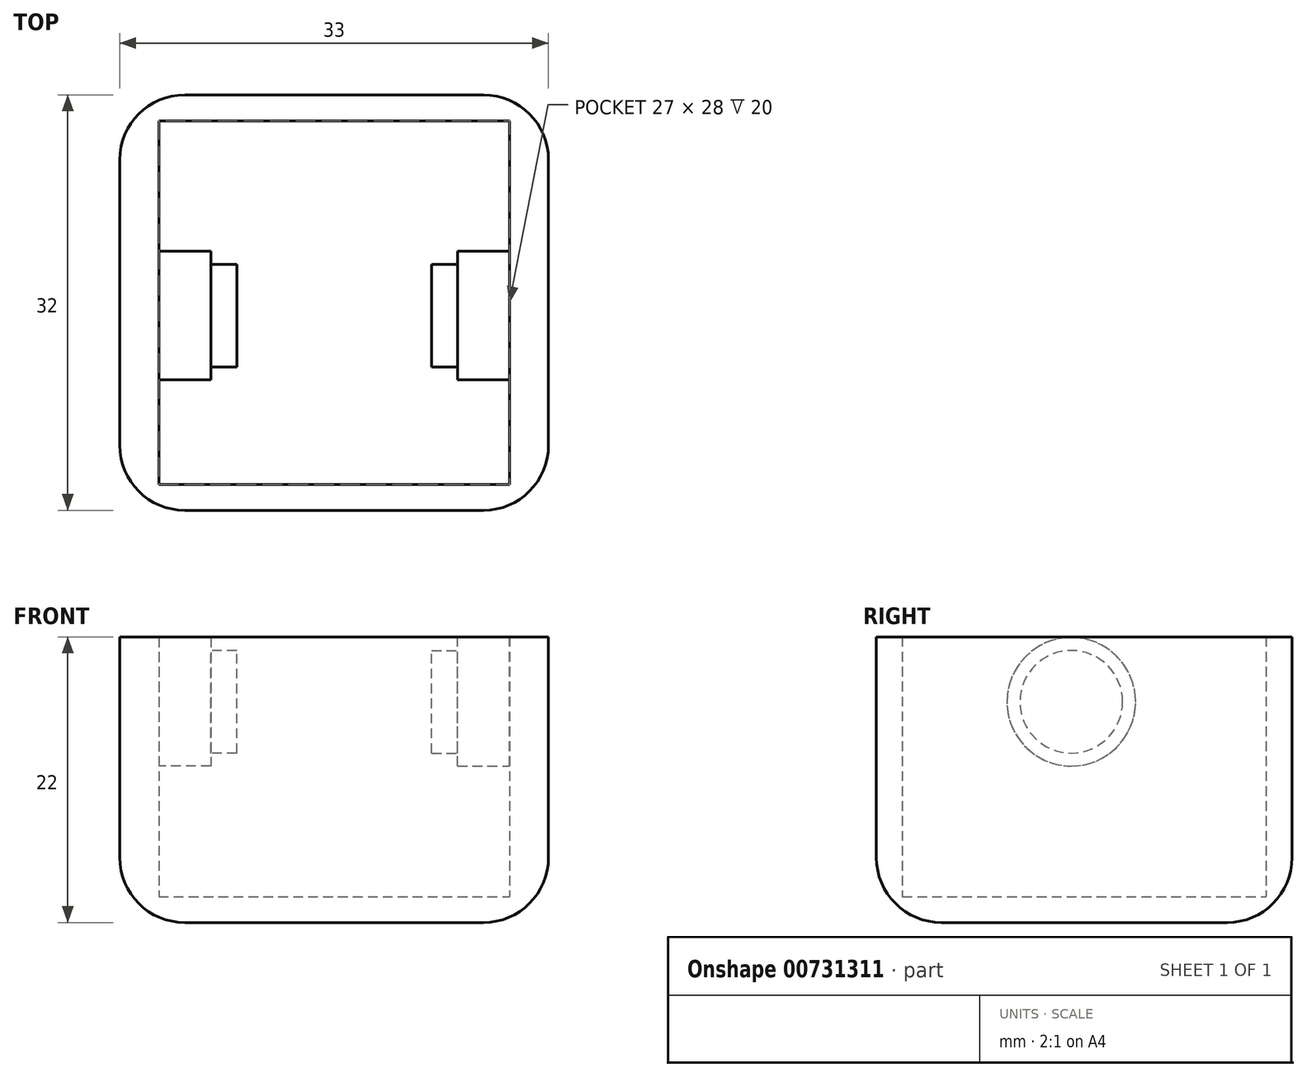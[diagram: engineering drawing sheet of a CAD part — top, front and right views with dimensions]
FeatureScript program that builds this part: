
annotation { "Feature Type Name" : "Feature", "Feature Type Description" : "" }
export const myFeature = defineFeature(function(context is Context, id is Id, definition is map)
    precondition{}
    {
        {
            var Q0;
            Q0=qCreatedBy(makeId("Top.planeOp"),FACE);
            var sketch = newSketch(context, id + "F0", { "sketchPlane" : qUnion([Q0])});
            skLineSegment(sketch, "E0.bottom", {"start": v(0, 32) * mm, "end": v(33, 32) * mm});
            skLineSegment(sketch, "E0.top", {"start": v(0, 0) * mm, "end": v(33, 0) * mm});
            skLineSegment(sketch, "E0.left", {"start": v(0, 32) * mm, "end": v(0, 0) * mm});
            skLineSegment(sketch, "E0.right", {"start": v(33, 32) * mm, "end": v(33, 0) * mm});
            skLineSegment(sketch, "E1", {"start": v(0, 16) * mm, "end": v(33, 16) * mm});
            skLineSegment(sketch, "E2", {"start": v(3, 16) * mm, "end": v(3, 32) * mm});
            skLineSegment(sketch, "E3", {"start": v(3, 30) * mm, "end": v(33, 30) * mm});
            skLineSegment(sketch, "E4", {"start": v(30, 30) * mm, "end": v(30, 0) * mm});
            skLineSegment(sketch, "E5.MirrorCS", {"start": v(3, 2) * mm, "end": v(33, 2) * mm});
            skLineSegment(sketch, "E6.MirrorCS", {"start": v(3, 16) * mm, "end": v(3, 0) * mm});
            skLineSegment(sketch, "E7", {"start": v(16.5, 16) * mm, "end": v(16.5, 26) * mm});
            skLineSegment(sketch, "E8", {"start": v(19.5, 26) * mm, "end": v(26.5, 26) * mm});
            skLineSegment(sketch, "E9", {"start": v(19.5, 16) * mm, "end": v(19.5, 26) * mm});
            skLineSegment(sketch, "E10", {"start": v(26.5, 16) * mm, "end": v(26.5, 26) * mm});
            skLineSegment(sketch, "E11.MirrorCS", {"start": v(19.5, 6) * mm, "end": v(26.5, 6) * mm});
            skLineSegment(sketch, "E12.MirrorCS", {"start": v(19.5, 16) * mm, "end": v(19.5, 6) * mm});
            skLineSegment(sketch, "E13.MirrorCS", {"start": v(26.5, 16) * mm, "end": v(26.5, 6) * mm});
            skLineSegment(sketch, "E14.MirrorCS", {"start": v(13.5, 16) * mm, "end": v(13.5, 6) * mm});
            skLineSegment(sketch, "E15.MirrorCS", {"start": v(13.5, 6) * mm, "end": v(6.5, 6) * mm});
            skLineSegment(sketch, "E16.MirrorCS", {"start": v(6.5, 16) * mm, "end": v(6.5, 6) * mm});
            skLineSegment(sketch, "E17.MirrorCS", {"start": v(6.5, 16) * mm, "end": v(6.5, 26) * mm});
            skLineSegment(sketch, "E18.MirrorCS", {"start": v(13.5, 26) * mm, "end": v(6.5, 26) * mm});
            skLineSegment(sketch, "E19.MirrorCS", {"start": v(13.5, 16) * mm, "end": v(13.5, 26) * mm});
            skLineSegment(sketch, "E20", {"start": v(3, 21) * mm, "end": v(0, 21) * mm});
            skLineSegment(sketch, "E21.MirrorCS", {"start": v(3, 11) * mm, "end": v(0, 11) * mm});
            skSolve(sketch);
        }
        {
            var Q0;
            {var subQ4=sQuery(id+"F0.wireOp",EDGE,"E20");Q0=makeQuery(id+"F0.imprint","IMPRINT",FACE,{"disambiguationData":[TD([[makeQuery(id+"F0.imprint","IMPRINT",EDGE,{"derivedFrom":subQ4}),-1.0]])]});}
            var Q1;
            {var subQ1=sQuery(id+"F0.wireOp",EDGE,"E0.bottom");var subQ5=sQuery(id+"F0.wireOp",EDGE,"E0.right");var subQ6=makeQuery(id+"F0.imprint","INTERSECT",VERTEX,{"derivedFrom":[subQ1,subQ5]});Q1=makeQuery(id+"F0.imprint","IMPRINT",FACE,{"disambiguationData":[TD([[makeQuery(id+"F0.imprint","IMPRINT",EDGE,{"disambiguationData":[TD([[subQ6,1.0]])],"derivedFrom":subQ1}),-1.0]])]});}
            var Q2;
            {var subQ0=sQuery(id+"F0.wireOp",EDGE,"E1");var subQ1=sQuery(id+"F0.wireOp",EDGE,"E0.right");var subQ2=makeQuery(id+"F0.imprint","INTERSECT",VERTEX,{"derivedFrom":[subQ1,subQ0]});Q2=makeQuery(id+"F0.imprint","IMPRINT",FACE,{"disambiguationData":[TD([[makeQuery(id+"F0.imprint","IMPRINT",EDGE,{"disambiguationData":[TD([[subQ2,1.0]])],"derivedFrom":subQ1}),-1.0]])]});}
            var Q3;
            {var subQ0=sQuery(id+"F0.wireOp",EDGE,"E1");var subQ1=sQuery(id+"F0.wireOp",EDGE,"E0.right");var subQ2=makeQuery(id+"F0.imprint","INTERSECT",VERTEX,{"derivedFrom":[subQ1,subQ0]});Q3=makeQuery(id+"F0.imprint","IMPRINT",FACE,{"disambiguationData":[TD([[makeQuery(id+"F0.imprint","IMPRINT",EDGE,{"disambiguationData":[TD([[subQ2,-1.0]])],"derivedFrom":subQ1}),-1.0]])]});}
            var Q4;
            {var subQ0=sQuery(id+"F0.wireOp",EDGE,"E0.right");var subQ1=sQuery(id+"F0.wireOp",EDGE,"E0.top");var subQ2=makeQuery(id+"F0.imprint","INTERSECT",VERTEX,{"derivedFrom":[subQ1,subQ0]});Q4=makeQuery(id+"F0.imprint","IMPRINT",FACE,{"disambiguationData":[TD([[makeQuery(id+"F0.imprint","IMPRINT",EDGE,{"disambiguationData":[TD([[subQ2,1.0]])],"derivedFrom":subQ1}),1.0]])]});}
            var Q5;
            {var subQ0=sQuery(id+"F0.wireOp",EDGE,"E4");var subQ1=sQuery(id+"F0.wireOp",EDGE,"E0.top");var subQ2=makeQuery(id+"F0.imprint","INTERSECT",VERTEX,{"derivedFrom":[subQ1,subQ0]});Q5=makeQuery(id+"F0.imprint","IMPRINT",FACE,{"disambiguationData":[TD([[makeQuery(id+"F0.imprint","IMPRINT",EDGE,{"disambiguationData":[TD([[subQ2,1.0]])],"derivedFrom":subQ1}),1.0]])]});}
            var Q6;
            {var subQ6=sQuery(id+"F0.wireOp",EDGE,"E21.MirrorCS");Q6=makeQuery(id+"F0.imprint","IMPRINT",FACE,{"disambiguationData":[TD([[makeQuery(id+"F0.imprint","IMPRINT",EDGE,{"derivedFrom":subQ6}),1.0]])]});}
            var Q7;
            {var subQ3=sQuery(id+"F0.wireOp",EDGE,"E21.MirrorCS");Q7=makeQuery(id+"F0.imprint","IMPRINT",FACE,{"disambiguationData":[TD([[makeQuery(id+"F0.imprint","IMPRINT",EDGE,{"derivedFrom":subQ3}),-1.0]])]});}
            var Q8;
            {var subQ3=sQuery(id+"F0.wireOp",EDGE,"E20");Q8=makeQuery(id+"F0.imprint","IMPRINT",FACE,{"disambiguationData":[TD([[makeQuery(id+"F0.imprint","IMPRINT",EDGE,{"derivedFrom":subQ3}),1.0]])]});}
            extrude(context, id + "F1", {"entities" : qUnion([Q0, Q1, Q2, Q3, Q4, Q5, Q6, Q7, Q8]), "depth" : 22 * mm, "offsetDistance" : 25 * mm});
        }
        {
            var Q0;
            Q0=makeQuery(id+"F0.imprint","IMPRINT",FACE,{"disambiguationData":[TD([[makeQuery(id+"F0.imprint","IMPRINT",EDGE,{"derivedFrom":sQuery(id+"F0.wireOp",EDGE,"E8")}),1.0]])]});
            var Q1;
            Q1=makeQuery(id+"F0.imprint","IMPRINT",FACE,{"disambiguationData":[TD([[makeQuery(id+"F0.imprint","IMPRINT",EDGE,{"derivedFrom":sQuery(id+"F0.wireOp",EDGE,"E11.MirrorCS")}),-1.0]])]});
            var Q2;
            {var subQ0=sQuery(id+"F0.wireOp",EDGE,"E14.MirrorCS");Q2=makeQuery(id+"F0.imprint","IMPRINT",FACE,{"disambiguationData":[TD([[makeQuery(id+"F0.imprint","IMPRINT",EDGE,{"derivedFrom":subQ0}),-1.0]])]});}
            var Q3;
            {var subQ2=sQuery(id+"F0.wireOp",EDGE,"E17.MirrorCS");Q3=makeQuery(id+"F0.imprint","IMPRINT",FACE,{"disambiguationData":[TD([[makeQuery(id+"F0.imprint","IMPRINT",EDGE,{"derivedFrom":subQ2}),-1.0]])]});}
            var Q4;
            Q4=makeQuery(id+"F0.imprint","IMPRINT",FACE,{"disambiguationData":[TD([[makeQuery(id+"F0.imprint","IMPRINT",EDGE,{"derivedFrom":sQuery(id+"F0.wireOp",EDGE,"E8")}),-1.0]])]});
            var Q5;
            Q5=makeQuery(id+"F0.imprint","IMPRINT",FACE,{"disambiguationData":[TD([[makeQuery(id+"F0.imprint","IMPRINT",EDGE,{"derivedFrom":sQuery(id+"F0.wireOp",EDGE,"E11.MirrorCS")}),1.0]])]});
            extrude(context, id + "F2", {"entities" : qUnion([Q0, Q1, Q2, Q3, Q4, Q5]), "operationType" : NewBodyOperationType.ADD, "depth" : 2 * mm, "offsetDistance" : 25 * mm});
        }
        {
            var Q0;
            Q0=qCreatedBy(makeId("Right.planeOp"),FACE);
            var sketch = newSketch(context, id + "F3", { "sketchPlane" : qUnion([Q0])});
            skLineSegment(sketch, "E22", {"start": v(0, 0) * mm, "end": v(0, 11) * mm});
            skCircle(sketch, "E23", {"center": v(15, 17) * mm, "radius": 3.95 * mm});
            skCircle(sketch, "E24.0", {"center": v(15, 17) * mm, "radius": 4.95 * mm});
            skSolve(sketch);
        }
        {
            var Q0;
            Q0=makeQuery(id+"F3.imprint","IMPRINT",FACE,{"disambiguationData":[TD([[makeQuery(id+"F3.imprint","IMPRINT",EDGE,{"derivedFrom":sQuery(id+"F3.wireOp",EDGE,"E23")}),1.0]])]});
            extrude(context, id + "F4", {"entities" : qUnion([Q0]), "operationType" : NewBodyOperationType.ADD, "depth" : 9 * mm, "offsetDistance" : 25 * mm});
        }
        {
            var Q0;
            Q0=makeQuery(id+"F1.opExtrude","CAP_EDGE",EDGE,{"disambiguationData":[OSD([sQuery(id+"F0.wireOp",EDGE,"E0.bottom")])],"isStart":true});
            var Q1;
            Q1=makeQuery(id+"F1.opExtrude","CAP_EDGE",EDGE,{"disambiguationData":[OSD([sQuery(id+"F0.wireOp",EDGE,"E0.left")])],"isStart":true});
            var Q2;
            Q2=makeQuery(id+"F1.opExtrude","CAP_EDGE",EDGE,{"disambiguationData":[OSD([sQuery(id+"F0.wireOp",EDGE,"E0.top")])],"isStart":true});
            var Q3;
            Q3=makeQuery(id+"F1.opExtrude","CAP_EDGE",EDGE,{"disambiguationData":[OSD([sQuery(id+"F0.wireOp",EDGE,"E0.right")])],"isStart":true});
            var Q4;
            Q4=makeQuery(id+"F1.opExtrude","SWEPT_EDGE",EDGE,{"disambiguationData":[OSD([sQuery(id+"F0.wireOp",EDGE,"E0.bottom"),sQuery(id+"F0.wireOp",EDGE,"E0.right")])]});
            var Q5;
            Q5=makeQuery(id+"F1.opExtrude","SWEPT_EDGE",EDGE,{"disambiguationData":[OSD([sQuery(id+"F0.wireOp",EDGE,"E0.bottom"),sQuery(id+"F0.wireOp",EDGE,"E0.left")])]});
            var Q6;
            Q6=makeQuery(id+"F1.opExtrude","SWEPT_EDGE",EDGE,{"disambiguationData":[OSD([sQuery(id+"F0.wireOp",EDGE,"E0.top"),sQuery(id+"F0.wireOp",EDGE,"E0.left")])]});
            var Q7;
            Q7=makeQuery(id+"F1.opExtrude","SWEPT_EDGE",EDGE,{"disambiguationData":[OSD([sQuery(id+"F0.wireOp",EDGE,"E0.top"),sQuery(id+"F0.wireOp",EDGE,"E0.right")])]});
            fillet(context, id + "F5", {"entities" : qUnion([Q0, Q1, Q2, Q3, Q4, Q5, Q6, Q7]), "radius" : 5 * mm, "tangentPropagation" : true, "allowEdgeOverflow" : false});
        }
        {
            var Q0;
            Q0=makeQuery(id+"F3.imprint","IMPRINT",FACE,{"disambiguationData":[TD([[makeQuery(id+"F3.imprint","IMPRINT",EDGE,{"derivedFrom":sQuery(id+"F3.wireOp",EDGE,"E23")}),-1.0]])]});
            extrude(context, id + "F6", {"entities" : qUnion([Q0]), "operationType" : NewBodyOperationType.ADD, "depth" : 7 * mm, "offsetDistance" : 25 * mm});
        }
        {
            var Q0;
            Q0=qCreatedBy(makeId("Right.planeOp"),FACE);
            cPlane(context, id + "F7", {"entities" : qUnion([Q0]), "cplaneType" : CPlaneType.OFFSET, "offset" : 16.5 * mm, "width" : 150 * mm, "height" : 150 * mm});
        }
        {
            var Q0;
            Q0=makeQuery(id+"F1.opExtrude","SWEPT_BODY",BODY,{"disambiguationData":[OSD([sQuery(id+"F0.wireOp",EDGE,"E0.bottom"),sQuery(id+"F0.wireOp",EDGE,"E0.top"),sQuery(id+"F0.wireOp",EDGE,"E0.left"),sQuery(id+"F0.wireOp",EDGE,"E0.right"),sQuery(id+"F0.wireOp",EDGE,"E2"),sQuery(id+"F0.wireOp",EDGE,"E3"),sQuery(id+"F0.wireOp",EDGE,"E4"),sQuery(id+"F0.wireOp",EDGE,"E5.MirrorCS"),sQuery(id+"F0.wireOp",EDGE,"E6.MirrorCS")])]});
            var Q1;
            Q1=qCreatedBy(id+"F7.planeOp",FACE);
            mirror(context, id + "F8", {"operationType" : NewBodyOperationType.ADD, "entities" : qUnion([Q0]), "mirrorPlane" : qUnion([Q1])});
        }
    });
